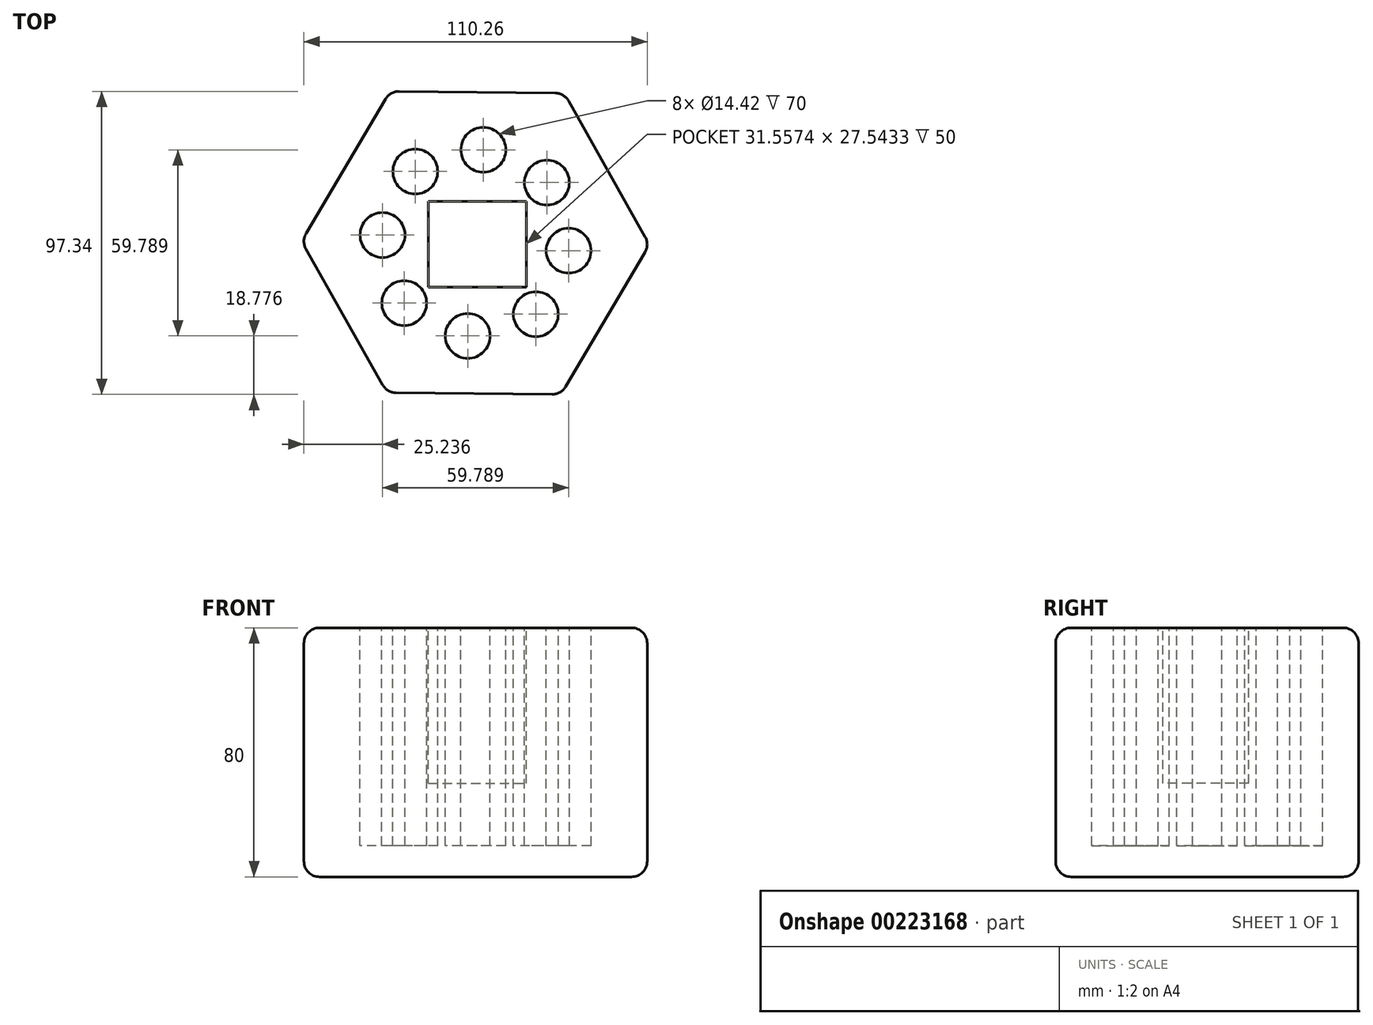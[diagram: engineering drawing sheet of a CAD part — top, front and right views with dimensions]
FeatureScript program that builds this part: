
annotation { "Feature Type Name" : "Feature", "Feature Type Description" : "" }
export const myFeature = defineFeature(function(context is Context, id is Id, definition is map)
    precondition{}
    {
        {
            var Q0;
            Q0=qCreatedBy(makeId("Top.planeOp"),FACE);
            var sketch = newSketch(context, id + "F0", { "sketchPlane" : qUnion([Q0])});
            skCircle(sketch, "E0.cCircle", {"center": v(0, 0) * mm, "radius": 48.41 * mm, "construction": true});
            skLineSegment(sketch, "E0.0", {"start": v(55.9, -0.57) * mm, "end": v(27.46, -48.7) * mm});
            skLineSegment(sketch, "E0.1", {"start": v(27.46, -48.7) * mm, "end": v(-28.44, -48.13) * mm});
            skLineSegment(sketch, "E0.2", {"start": v(-28.44, -48.13) * mm, "end": v(-55.9, 0.57) * mm});
            skLineSegment(sketch, "E0.3", {"start": v(-55.9, 0.57) * mm, "end": v(-27.46, 48.7) * mm});
            skLineSegment(sketch, "E0.4", {"start": v(-27.46, 48.7) * mm, "end": v(28.44, 48.13) * mm});
            skLineSegment(sketch, "E0.5", {"start": v(28.44, 48.13) * mm, "end": v(55.9, -0.57) * mm});
            skPoint(sketch, "E0.0.midPoint", {"position": v(41.68, -24.63) * mm});
            skSolve(sketch);
        }
        {
            var Q0;
            Q0 = qSketchRegion(id + "F0", true);
            extrude(context, id + "F1", {"entities" : qUnion([Q0]), "oppositeDirection" : true, "depth" : 80 * mm});
        }
        {
            var Q0;
            Q0=makeQuery(id+"F1.opExtrude","SWEPT_EDGE",EDGE,{"disambiguationData":[OSD([sQuery(id+"F0.wireOp",EDGE,"E0.0"),sQuery(id+"F0.wireOp",EDGE,"E0.5")])]});
            var Q1;
            Q1=makeQuery(id+"F1.opExtrude","SWEPT_EDGE",EDGE,{"disambiguationData":[OSD([sQuery(id+"F0.wireOp",EDGE,"E0.0"),sQuery(id+"F0.wireOp",EDGE,"E0.1")])]});
            var Q2;
            Q2=makeQuery(id+"F1.opExtrude","CAP_EDGE",EDGE,{"disambiguationData":[OSD([sQuery(id+"F0.wireOp",EDGE,"E0.0")])],"isStart":false});
            var Q3;
            Q3=makeQuery(id+"F1.opExtrude","CAP_EDGE",EDGE,{"disambiguationData":[OSD([sQuery(id+"F0.wireOp",EDGE,"E0.0")])],"isStart":true});
            var Q4;
            Q4=makeQuery(id+"F1.opExtrude","CAP_EDGE",EDGE,{"disambiguationData":[OSD([sQuery(id+"F0.wireOp",EDGE,"E0.1")])],"isStart":true});
            var Q5;
            Q5=makeQuery(id+"F1.opExtrude","CAP_EDGE",EDGE,{"disambiguationData":[OSD([sQuery(id+"F0.wireOp",EDGE,"E0.1")])],"isStart":false});
            var Q6;
            Q6=makeQuery(id+"F1.opExtrude","SWEPT_EDGE",EDGE,{"disambiguationData":[OSD([sQuery(id+"F0.wireOp",EDGE,"E0.1"),sQuery(id+"F0.wireOp",EDGE,"E0.2")])]});
            var Q7;
            Q7=makeQuery(id+"F1.opExtrude","CAP_EDGE",EDGE,{"disambiguationData":[OSD([sQuery(id+"F0.wireOp",EDGE,"E0.5")])],"isStart":false});
            var Q8;
            Q8=makeQuery(id+"F1.opExtrude","CAP_EDGE",EDGE,{"disambiguationData":[OSD([sQuery(id+"F0.wireOp",EDGE,"E0.5")])],"isStart":true});
            var Q9;
            Q9=makeQuery(id+"F1.opExtrude","SWEPT_EDGE",EDGE,{"disambiguationData":[OSD([sQuery(id+"F0.wireOp",EDGE,"E0.4"),sQuery(id+"F0.wireOp",EDGE,"E0.5")])]});
            var Q10;
            Q10=makeQuery(id+"F1.opExtrude","CAP_EDGE",EDGE,{"disambiguationData":[OSD([sQuery(id+"F0.wireOp",EDGE,"E0.4")])],"isStart":true});
            var Q11;
            Q11=makeQuery(id+"F1.opExtrude","CAP_EDGE",EDGE,{"disambiguationData":[OSD([sQuery(id+"F0.wireOp",EDGE,"E0.3")])],"isStart":true});
            var Q12;
            Q12=makeQuery(id+"F1.opExtrude","CAP_EDGE",EDGE,{"disambiguationData":[OSD([sQuery(id+"F0.wireOp",EDGE,"E0.2")])],"isStart":true});
            var Q13;
            Q13=makeQuery(id+"F1.opExtrude","CAP_FACE",FACE,{"disambiguationData":[OSD([sQuery(id+"F0.wireOp",EDGE,"E0.0"),sQuery(id+"F0.wireOp",EDGE,"E0.1"),sQuery(id+"F0.wireOp",EDGE,"E0.2"),sQuery(id+"F0.wireOp",EDGE,"E0.3"),sQuery(id+"F0.wireOp",EDGE,"E0.4"),sQuery(id+"F0.wireOp",EDGE,"E0.5")])],"isStart":false});
            var Q14;
            Q14=makeQuery(id+"F1.opExtrude","SWEPT_EDGE",EDGE,{"disambiguationData":[OSD([sQuery(id+"F0.wireOp",EDGE,"E0.2"),sQuery(id+"F0.wireOp",EDGE,"E0.3")])]});
            var Q15;
            Q15=makeQuery(id+"F1.opExtrude","SWEPT_EDGE",EDGE,{"disambiguationData":[OSD([sQuery(id+"F0.wireOp",EDGE,"E0.3"),sQuery(id+"F0.wireOp",EDGE,"E0.4")])]});
            fillet(context, id + "F2", {"entities" : qUnion([Q0, Q1, Q2, Q3, Q4, Q5, Q6, Q7, Q8, Q9, Q10, Q11, Q12, Q13, Q14, Q15]), "radius" : 5 * mm, "tangentPropagation" : true, "allowEdgeOverflow" : false});
        }
        {
            var Q0;
            Q0=makeQuery(id+"F1.opExtrude","CAP_FACE",FACE,{"disambiguationData":[OSD([sQuery(id+"F0.wireOp",EDGE,"E0.0"),sQuery(id+"F0.wireOp",EDGE,"E0.1"),sQuery(id+"F0.wireOp",EDGE,"E0.2"),sQuery(id+"F0.wireOp",EDGE,"E0.3"),sQuery(id+"F0.wireOp",EDGE,"E0.4"),sQuery(id+"F0.wireOp",EDGE,"E0.5")])],"isStart":true});
            var sketch = newSketch(context, id + "F3", { "sketchPlane" : qUnion([Q0])});
            skCircle(sketch, "E1", {"center": v(-19.36, 22.92) * mm, "radius": 7.21 * mm});
            skCircle(sketch, "E2.1.0", {"center": v(-29.9, 2.51) * mm, "radius": 7.21 * mm});
            skCircle(sketch, "E2.2.0", {"center": v(-22.92, -19.36) * mm, "radius": 7.21 * mm});
            skCircle(sketch, "E2.3.0", {"center": v(-2.51, -29.9) * mm, "radius": 7.21 * mm});
            skCircle(sketch, "E2.4.0", {"center": v(19.36, -22.92) * mm, "radius": 7.21 * mm});
            skCircle(sketch, "E2.5.0", {"center": v(29.9, -2.51) * mm, "radius": 7.21 * mm});
            skCircle(sketch, "E2.6.0", {"center": v(22.92, 19.36) * mm, "radius": 7.21 * mm});
            skCircle(sketch, "E2.7.0", {"center": v(2.51, 29.9) * mm, "radius": 7.21 * mm});
            skPoint(sketch, "E2.center", {"position": v(0, 0) * mm});
            skSolve(sketch);
        }
        {
            var Q0;
            Q0 = qSketchRegion(id + "F3", true);
            extrude(context, id + "F4", {"entities" : qUnion([Q0]), "operationType" : NewBodyOperationType.ADD, "oppositeDirection" : true, "depth" : 50 * mm});
        }
        {
            var Q0;
            Q0=makeQuery(id+"F3.imprint","IMPRINT",FACE,{"disambiguationData":[TD([[makeQuery(id+"F3.imprint","IMPRINT",EDGE,{"derivedFrom":sQuery(id+"F3.wireOp",EDGE,"E2.1.0")}),1.0]])]});
            var Q1;
            Q1=makeQuery(id+"F3.imprint","IMPRINT",FACE,{"disambiguationData":[TD([[makeQuery(id+"F3.imprint","IMPRINT",EDGE,{"derivedFrom":sQuery(id+"F3.wireOp",EDGE,"E2.2.0")}),1.0]])]});
            var Q2;
            Q2=makeQuery(id+"F3.imprint","IMPRINT",FACE,{"disambiguationData":[TD([[makeQuery(id+"F3.imprint","IMPRINT",EDGE,{"derivedFrom":sQuery(id+"F3.wireOp",EDGE,"E2.4.0")}),1.0]])]});
            var Q3;
            Q3=makeQuery(id+"F3.imprint","IMPRINT",FACE,{"disambiguationData":[TD([[makeQuery(id+"F3.imprint","IMPRINT",EDGE,{"derivedFrom":sQuery(id+"F3.wireOp",EDGE,"E2.7.0")}),1.0]])]});
            var Q4;
            Q4=makeQuery(id+"F3.imprint","IMPRINT",FACE,{"disambiguationData":[TD([[makeQuery(id+"F3.imprint","IMPRINT",EDGE,{"derivedFrom":sQuery(id+"F3.wireOp",EDGE,"E2.3.0")}),1.0]])]});
            var Q5;
            Q5=makeQuery(id+"F3.imprint","IMPRINT",FACE,{"disambiguationData":[TD([[makeQuery(id+"F3.imprint","IMPRINT",EDGE,{"derivedFrom":sQuery(id+"F3.wireOp",EDGE,"E1")}),1.0]])]});
            var Q6;
            Q6=makeQuery(id+"F3.imprint","IMPRINT",FACE,{"disambiguationData":[TD([[makeQuery(id+"F3.imprint","IMPRINT",EDGE,{"derivedFrom":sQuery(id+"F3.wireOp",EDGE,"E2.6.0")}),1.0]])]});
            var Q7;
            Q7=makeQuery(id+"F3.imprint","IMPRINT",FACE,{"disambiguationData":[TD([[makeQuery(id+"F3.imprint","IMPRINT",EDGE,{"derivedFrom":sQuery(id+"F3.wireOp",EDGE,"E2.5.0")}),1.0]])]});
            var Q8;
            Q8=sQuery(id+"F3.wireOp",EDGE,"E2.1.0");
            extrude(context, id + "F5", {"entities" : qUnion([Q0, Q1, Q2, Q3, Q4, Q5, Q6, Q7]), "operationType" : NewBodyOperationType.REMOVE, "surfaceEntities" : qUnion([Q8]), "oppositeDirection" : true, "depth" : 70 * mm});
        }
        {
            var Q0;
            Q0=makeQuery(id+"F3.imprint","IMPRINT",FACE,{"disambiguationData":[TD([[makeQuery(id+"F3.imprint","IMPRINT",EDGE,{"derivedFrom":sQuery(id+"F3.wireOp",EDGE,"E1")}),-1.0]])]});
            var sketch = newSketch(context, id + "F6", { "sketchPlane" : qUnion([Q0])});
            skLineSegment(sketch, "E3.bottom", {"start": v(-15.2, 13.35) * mm, "end": v(16.35, 13.35) * mm});
            skLineSegment(sketch, "E3.top", {"start": v(-15.2, -14.2) * mm, "end": v(16.35, -14.2) * mm});
            skLineSegment(sketch, "E3.left", {"start": v(-15.2, 13.35) * mm, "end": v(-15.2, -14.2) * mm});
            skLineSegment(sketch, "E3.right", {"start": v(16.35, 13.35) * mm, "end": v(16.35, -14.2) * mm});
            skSolve(sketch);
        }
        {
            var Q0;
            Q0 = qSketchRegion(id + "F6", true);
            extrude(context, id + "F7", {"entities" : qUnion([Q0]), "operationType" : NewBodyOperationType.REMOVE, "oppositeDirection" : true, "depth" : 50 * mm});
        }
    });
